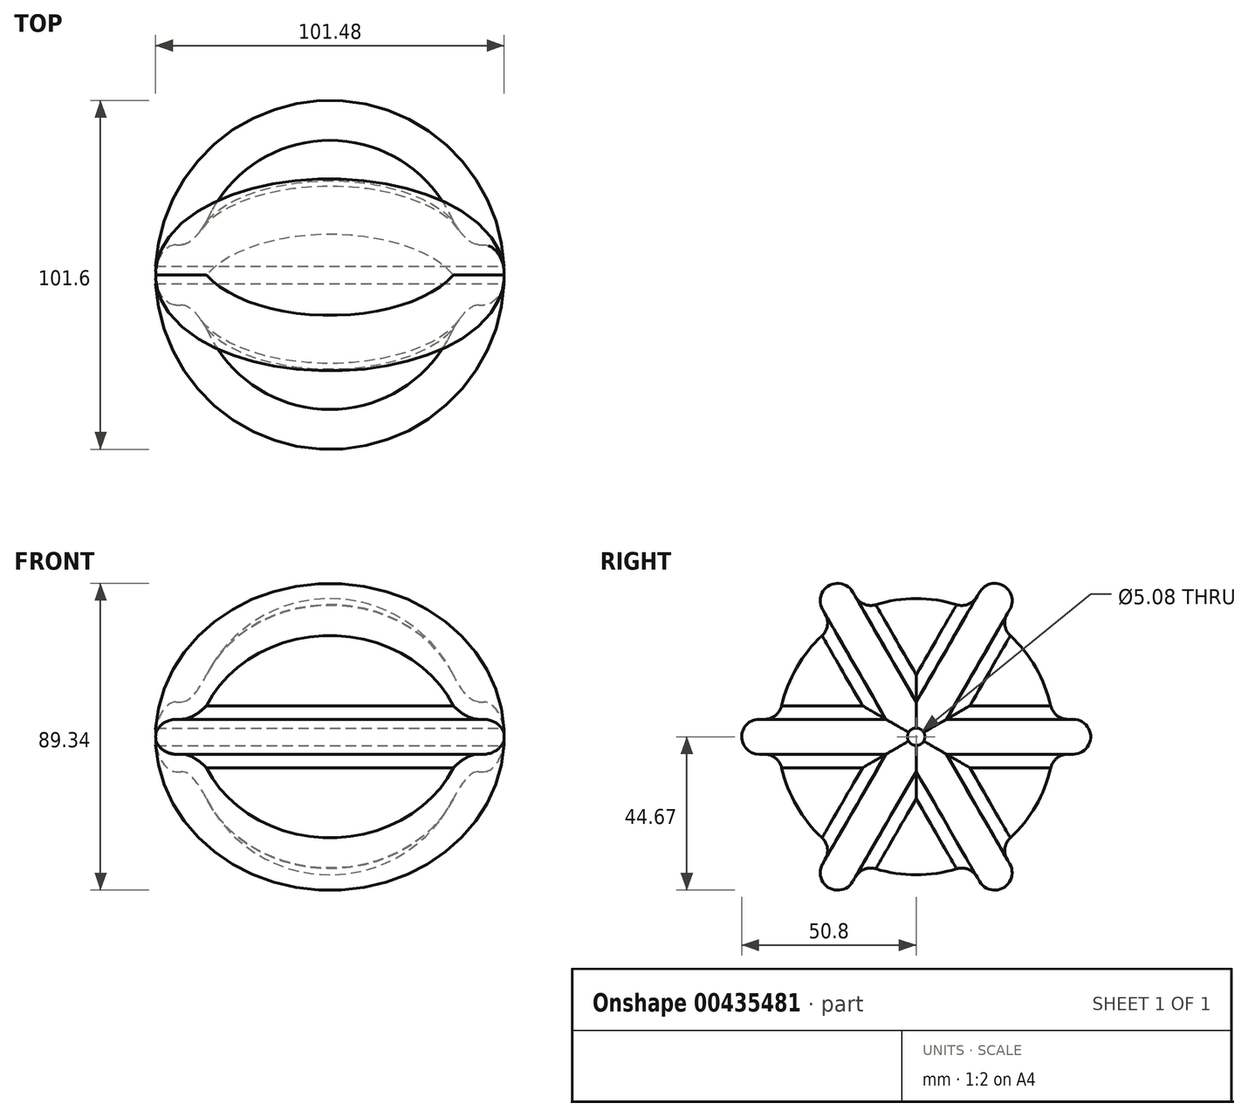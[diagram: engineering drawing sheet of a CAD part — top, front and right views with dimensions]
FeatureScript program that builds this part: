
annotation { "Feature Type Name" : "Feature", "Feature Type Description" : "" }
export const myFeature = defineFeature(function(context is Context, id is Id, definition is map)
    precondition{}
    {
        {
            var Q0;
            Q0=qCreatedBy(makeId("Top.planeOp"),FACE);
            var sketch = newSketch(context, id + "F0", { "sketchPlane" : qUnion([Q0])});
            skArc(sketch, "E0", {"start": v(40.21, 0) * mm, "mid": v(0, 40.21) * mm, "end": v(-40.21, 0) * mm});
            skLineSegment(sketch, "E1", {"start": v(0, 0) * mm, "end": v(14.76, 0) * mm, "construction": true});
            skLineSegment(sketch, "E2", {"start": v(-44.3, 0) * mm, "end": v(46.06, 0) * mm});
            skLineSegment(sketch, "E3", {"start": v(0, -0.36) * mm, "end": v(0, 0) * mm});
            skLineSegment(sketch, "E4", {"start": v(0, -8.12) * mm, "end": v(0, 10.7) * mm});
            skSolve(sketch);
        }
        {
            var Q0;
            {var subQ0=sQuery(id+"F0.wireOp",EDGE,"E0");Q0=makeQuery(id+"F0.imprint","IMPRINT",FACE,{"disambiguationData":[TD([[makeQuery(id+"F0.imprint","IMPRINT",EDGE,{"derivedFrom":subQ0}),1.0]])]});}
            var Q1;
            Q1=sQuery(id+"F0.wireOp",EDGE,"E2");
            revolve(context, id + "F1", {"entities" : qUnion([Q0]), "axis" : qUnion([Q1]), "revolveType" : RevolveType.ONE_DIRECTION, "angle" : 360 * degree});
        }
        {
            var Q0;
            Q0=qCreatedBy(makeId("Top.planeOp"),FACE);
            var sketch = newSketch(context, id + "F2", { "sketchPlane" : qUnion([Q0])});
            skCircle(sketch, "E5", {"center": v(0, 0) * mm, "radius": 50.8 * mm});
            skSolve(sketch);
        }
        {
            var Q0;
            Q0=makeQuery(id+"F2.imprint","IMPRINT",FACE,{"disambiguationData":[TD([[makeQuery(id+"F2.imprint","IMPRINT",EDGE,{"derivedFrom":sQuery(id+"F2.wireOp",EDGE,"E5")}),1.0]])]});
            var Q1;
            Q1=sQuery(id+"F2.wireOp",EDGE,"E5");
            extrude(context, id + "F3", {"entities" : qUnion([Q0]), "operationType" : NewBodyOperationType.ADD, "surfaceEntities" : qUnion([Q1]), "depth" : 5.08 * mm, "hasSecondDirection" : true, "secondDirectionOppositeDirection" : true, "secondDirectionDepth" : 5.08 * mm});
        }
        {
            var Q0;
            Q0=makeQuery(id+"F3.opExtrude","CAP_FACE",FACE,{"disambiguationData":[OSD([sQuery(id+"F2.wireOp",EDGE,"E5")])],"isStart":false});
            fillet(context, id + "F4", {"entities" : qUnion([Q0]), "radius" : 5.08 * mm, "tangentPropagation" : true, "allowEdgeOverflow" : false});
        }
        {
            var Q0;
            Q0=makeQuery(id+"F3.opExtrude","CAP_FACE",FACE,{"disambiguationData":[OSD([sQuery(id+"F2.wireOp",EDGE,"E5")])],"isStart":true});
            fillet(context, id + "F5", {"entities" : qUnion([Q0]), "radius" : 5.08 * mm, "tangentPropagation" : true, "allowEdgeOverflow" : false});
        }
        {
            var Q0;
            Q0=makeQuery(id+"F1.opRevolve","SWEPT_BODY",BODY,{"disambiguationData":[OSD([sQuery(id+"F0.wireOp",EDGE,"E0"),sQuery(id+"F0.wireOp",EDGE,"E2")])]});
            var Q1;
            Q1=sQuery(id+"F0.wireOp",EDGE,"E2");
            circularPattern(context, id + "F6", {"operationType" : NewBodyOperationType.ADD, "entities" : qUnion([Q0]), "axis" : qUnion([Q1]), "angle" : 180 * degree, "instanceCount" : 4, "equalSpace" : true, "isCentered" : true});
        }
        {
            var Q0;
            Q0=qCreatedBy(makeId("Right.planeOp"),FACE);
            var sketch = newSketch(context, id + "F7", { "sketchPlane" : qUnion([Q0])});
            skCircle(sketch, "E6", {"center": v(0, 0) * mm, "radius": 2.54 * mm});
            skSolve(sketch);
        }
        {
            var Q0;
            Q0 = qSketchRegion(id + "F7", true);
            var Q1;
            Q1=sQuery(id+"F7.wireOp",EDGE,"E6");
            extrude(context, id + "F8", {"entities" : qUnion([Q0]), "operationType" : NewBodyOperationType.REMOVE, "surfaceEntities" : qUnion([Q1]), "endBound" : BoundingType.SYMMETRIC, "oppositeDirection" : true, "depth" : 101.6 * mm});
        }
    });
